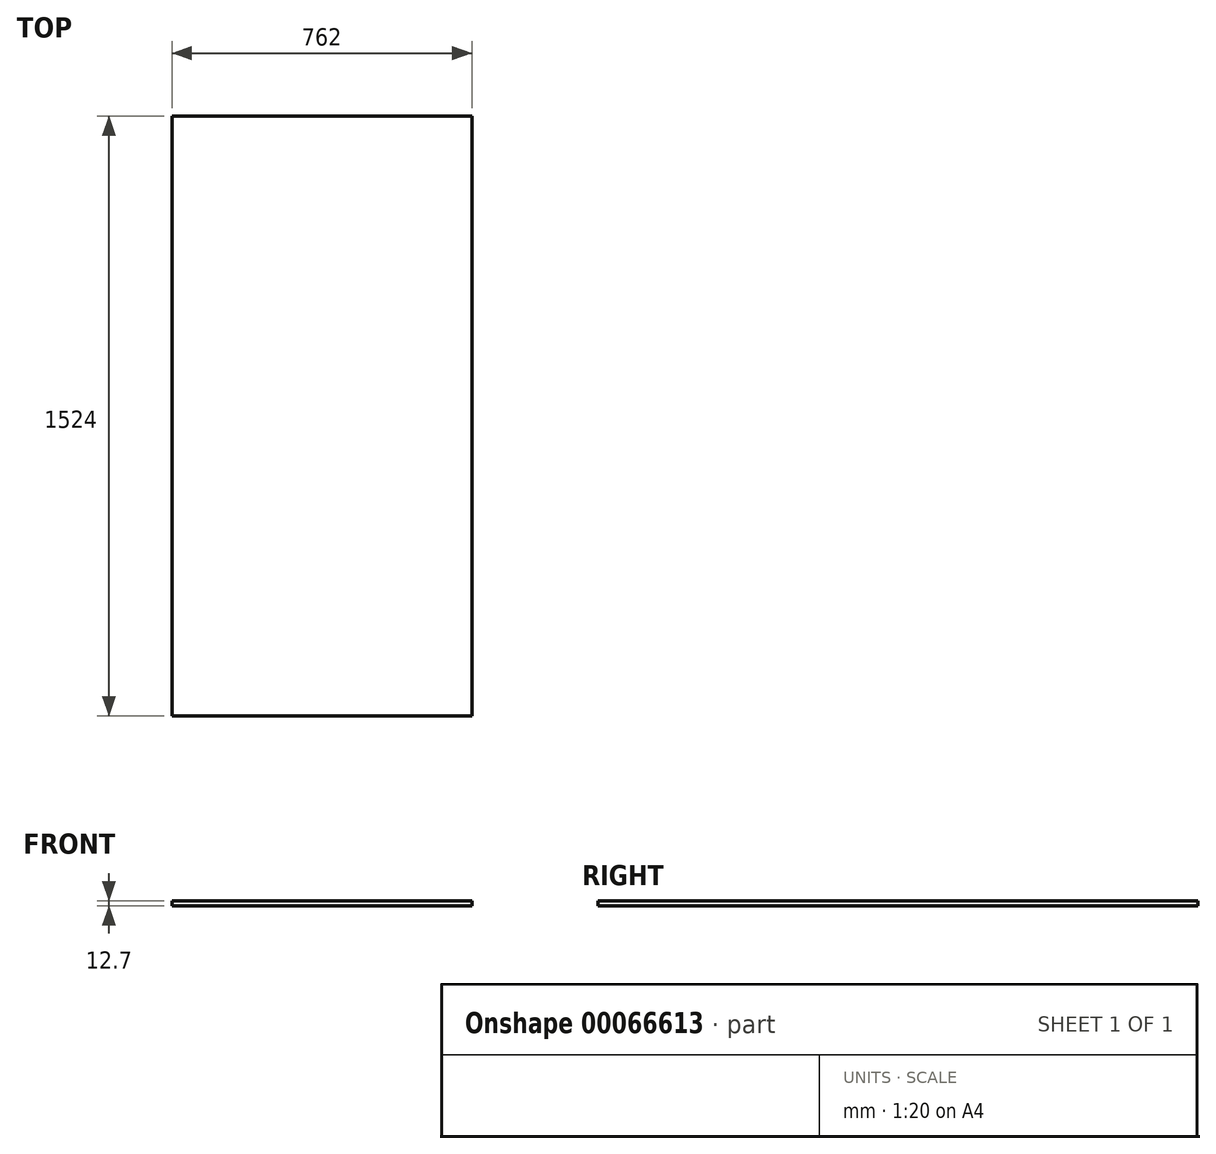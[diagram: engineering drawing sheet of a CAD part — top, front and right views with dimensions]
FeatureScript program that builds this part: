
annotation { "Feature Type Name" : "Feature", "Feature Type Description" : "" }
export const myFeature = defineFeature(function(context is Context, id is Id, definition is map)
    precondition{}
    {
        {
            var Q0;
            Q0=qCreatedBy(makeId("Top.planeOp"),FACE);
            var sketch = newSketch(context, id + "F0", { "sketchPlane" : qUnion([Q0])});
            skLineSegment(sketch, "E0.rect.bottom", {"start": v(-381, -762) * mm, "end": v(381, -762) * mm});
            skLineSegment(sketch, "E0.rect.top", {"start": v(-381, 762) * mm, "end": v(381, 762) * mm});
            skLineSegment(sketch, "E0.rect.left", {"start": v(-381, -762) * mm, "end": v(-381, 762) * mm});
            skLineSegment(sketch, "E0.rect.right", {"start": v(381, -762) * mm, "end": v(381, 762) * mm});
            skPoint(sketch, "E0.rect.middle", {"position": v(0, 0) * mm});
            skSolve(sketch);
        }
        {
            var Q0;
            Q0 = qSketchRegion(id + "F0", true);
            extrude(context, id + "F1", {"entities" : qUnion([Q0]), "depth" : 12.7 * mm});
        }
    });
